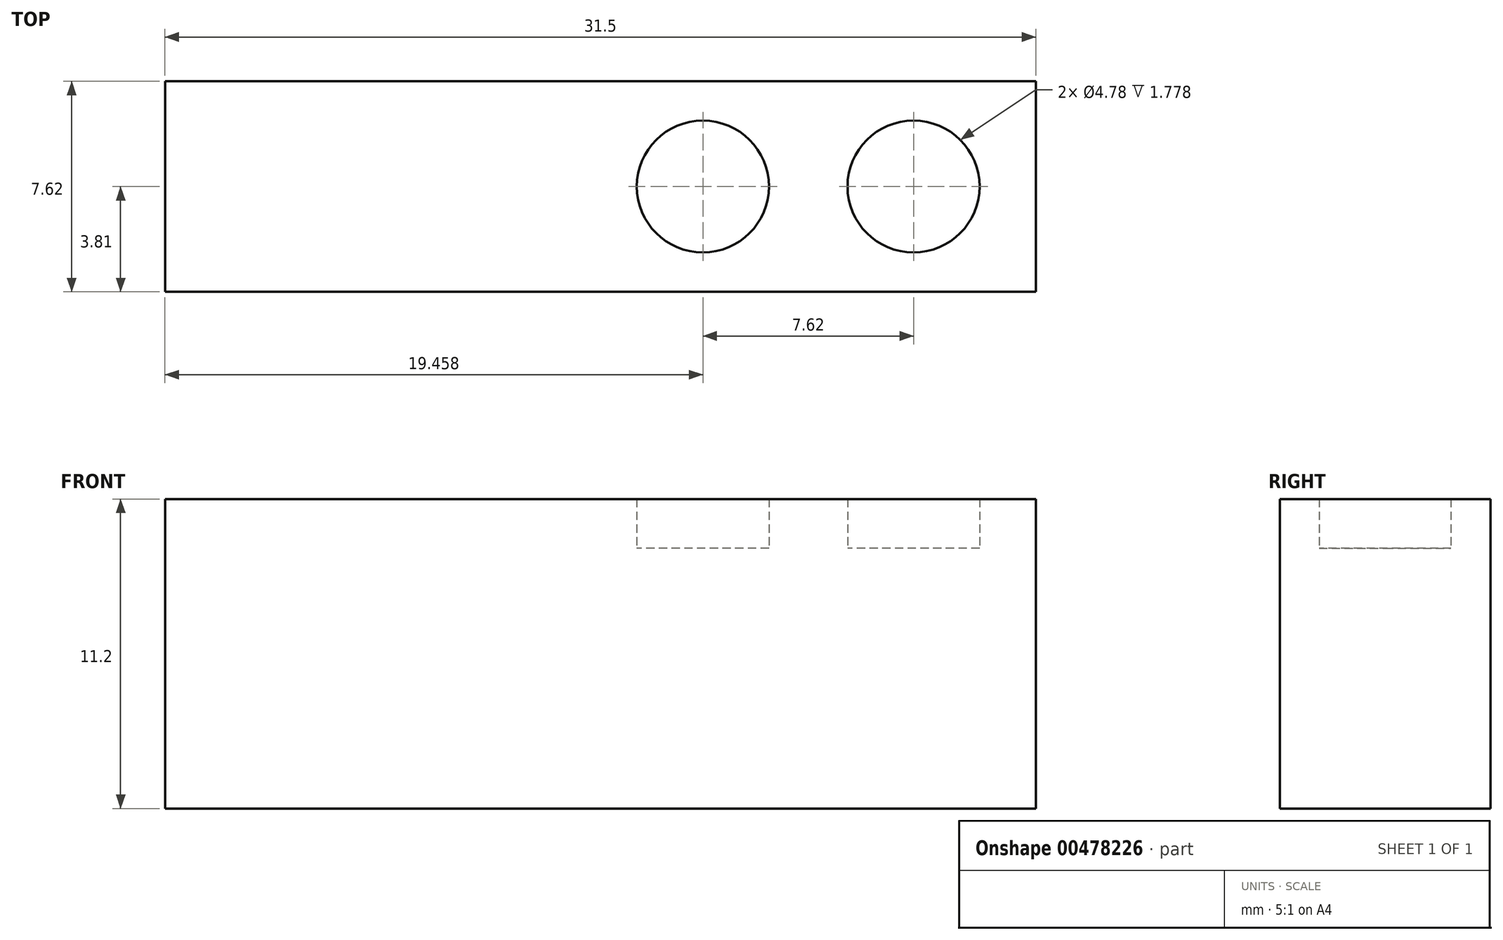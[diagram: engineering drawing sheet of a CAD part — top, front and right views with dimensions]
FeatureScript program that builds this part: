
annotation { "Feature Type Name" : "Feature", "Feature Type Description" : "" }
export const myFeature = defineFeature(function(context is Context, id is Id, definition is map)
    precondition{}
    {
        {
            var Q0;
            Q0=qCreatedBy(makeId("Top.planeOp"),FACE);
            var sketch = newSketch(context, id + "F0", { "sketchPlane" : qUnion([Q0])});
            skLineSegment(sketch, "E0.bottom", {"start": v(-15.75, 3.8) * mm, "end": v(15.75, 3.8) * mm});
            skLineSegment(sketch, "E0.top", {"start": v(-15.75, -3.8) * mm, "end": v(15.75, -3.8) * mm});
            skLineSegment(sketch, "E0.left", {"start": v(-15.75, 3.8) * mm, "end": v(-15.75, -3.8) * mm});
            skLineSegment(sketch, "E0.right", {"start": v(15.75, 3.8) * mm, "end": v(15.75, -3.8) * mm});
            skPoint(sketch, "E0.middle", {"position": v(0, 0) * mm});
            skSolve(sketch);
        }
        {
            var Q0;
            Q0=makeQuery(id+"F0.imprint","IMPRINT",FACE,{"disambiguationData":[TD([[makeQuery(id+"F0.imprint","IMPRINT",EDGE,{"derivedFrom":sQuery(id+"F0.wireOp",EDGE,"E0.bottom")}),-1.0]])]});
            extrude(context, id + "F1", {"entities" : qUnion([Q0]), "depth" : 9.42 * mm});
        }
        {
            var Q0;
            Q0=makeQuery(id+"F1.opExtrude","CAP_FACE",FACE,{"disambiguationData":[OSD([sQuery(id+"F0.wireOp",EDGE,"E0.bottom"),sQuery(id+"F0.wireOp",EDGE,"E0.top"),sQuery(id+"F0.wireOp",EDGE,"E0.left"),sQuery(id+"F0.wireOp",EDGE,"E0.right")])],"isStart":false});
            var sketch = newSketch(context, id + "F2", { "sketchPlane" : qUnion([Q0])});
            skCircle(sketch, "E1", {"center": v(-11.33, 0) * mm, "radius": 2.39 * mm});
            skCircle(sketch, "E2", {"center": v(-3.7, 0) * mm, "radius": 2.39 * mm});
            skCircle(sketch, "E3.MirrorC", {"center": v(3.7, 0) * mm, "radius": 2.39 * mm});
            skCircle(sketch, "E4.MirrorC", {"center": v(11.33, 0) * mm, "radius": 2.39 * mm});
            skSolve(sketch);
        }
        {
            var Q0;
            Q0=makeQuery(id+"F2.imprint","IMPRINT",FACE,{"disambiguationData":[TD([[makeQuery(id+"F2.imprint","IMPRINT",EDGE,{"derivedFrom":sQuery(id+"F2.wireOp",EDGE,"E4.MirrorC")}),-1.0]])]});
            var Q1;
            Q1=makeQuery(id+"F2.imprint","IMPRINT",FACE,{"disambiguationData":[TD([[makeQuery(id+"F2.imprint","IMPRINT",EDGE,{"derivedFrom":sQuery(id+"F2.wireOp",EDGE,"E3.MirrorC")}),-1.0]])]});
            var Q2;
            Q2=makeQuery(id+"F2.imprint","IMPRINT",FACE,{"disambiguationData":[TD([[makeQuery(id+"F2.imprint","IMPRINT",EDGE,{"derivedFrom":sQuery(id+"F2.wireOp",EDGE,"E2")}),1.0]])]});
            var Q3;
            Q3=makeQuery(id+"F2.imprint","IMPRINT",FACE,{"disambiguationData":[TD([[makeQuery(id+"F2.imprint","IMPRINT",EDGE,{"derivedFrom":sQuery(id+"F2.wireOp",EDGE,"E1")}),1.0]])]});
            extrude(context, id + "F3", {"entities" : qUnion([Q0, Q1, Q2, Q3]), "operationType" : NewBodyOperationType.ADD, "depth" : 1.78 * mm});
        }
    });
